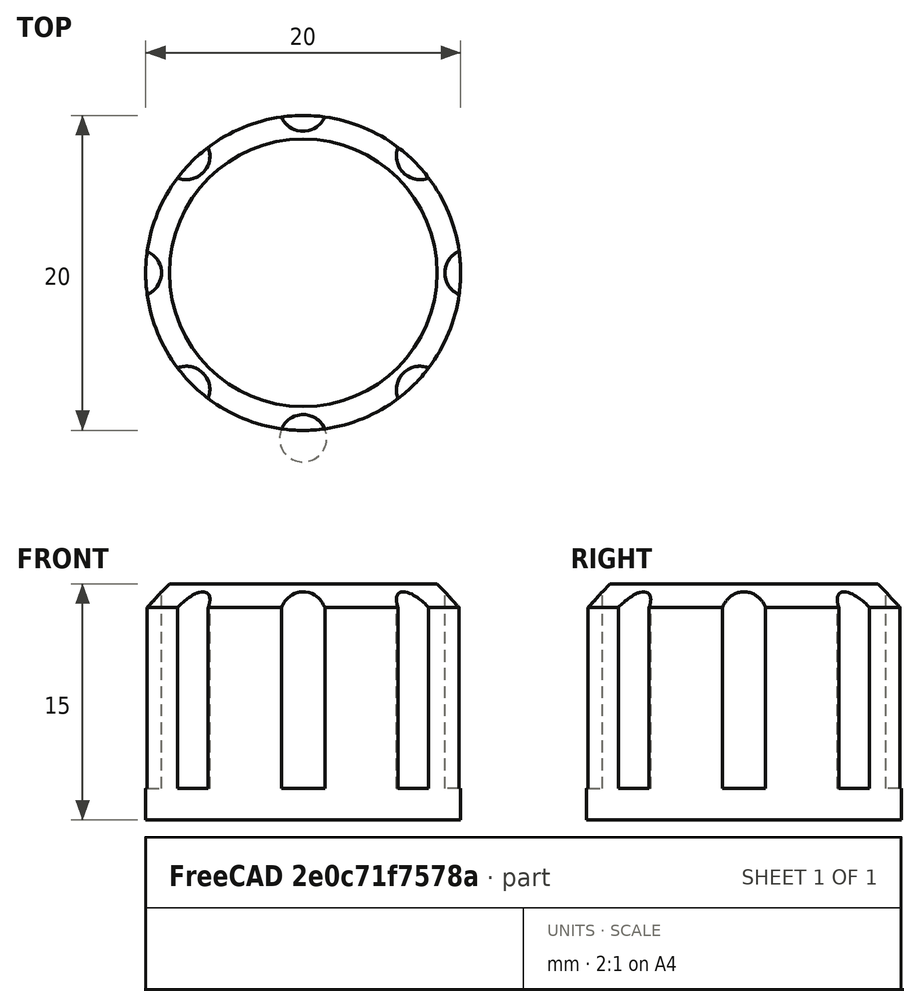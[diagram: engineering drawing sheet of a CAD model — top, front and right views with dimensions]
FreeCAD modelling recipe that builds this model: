
FCSTD DOCUMENT  (FreeCAD 0.16R6707 (Git))
Label: Boton
License: CreativeCommons Attribution-ShareAlike
LicenseURL: http://creativecommons.org/licenses/by-sa/4.0/
objects: Part::Cylinder×2, Part::FeaturePython×1, Part::Chamfer×1, Part::Cut×1
note: 5 computed .brp shape members not serialized (recipe doc carries the construction recipe); baked Part::Feature solids carry a one-line shape summary decoded from their .brp

FEATURE [Part::Cylinder] Cylinder  label="Base_boton"
  Angle = 360
  Height = 15
  Radius = 10
FEATURE [Part::Cylinder] Cylinder001  label="Hendiduras"
  Angle = 360
  Height = 17
  Placement = pos=(10.5,0,3) rot=(0,0,1;0rad)
  Radius = 1.5
FEATURE [Part::FeaturePython] Array  label="Array_hendiduras"  # Draft array (typed FeaturePython)
  Angle = 360
  ArrayType = 1
  Axis = (0,0,1)
  Base = -> Cylinder001
  Center = (0,0,0)
  Fuse = false
  IntervalAxis = (0,0,0)
  IntervalX = (1,0,0)
  IntervalY = (0,1,0)
  IntervalZ = (0,0,0)
  NumberPolar = 8
  NumberX = 1
  NumberY = 1
  NumberZ = 1
  Placement = pos=(0,0,-1) rot=(0,0,1;0rad)
FEATURE [Part::Chamfer] Chamfer
  Base = -> Cylinder
  Edges = 1 edges r=1.5: [Edge1]
FEATURE [Part::Cut] Cut  label="Boton_Acabado"
  Base = -> Chamfer
  Tool = -> Array
